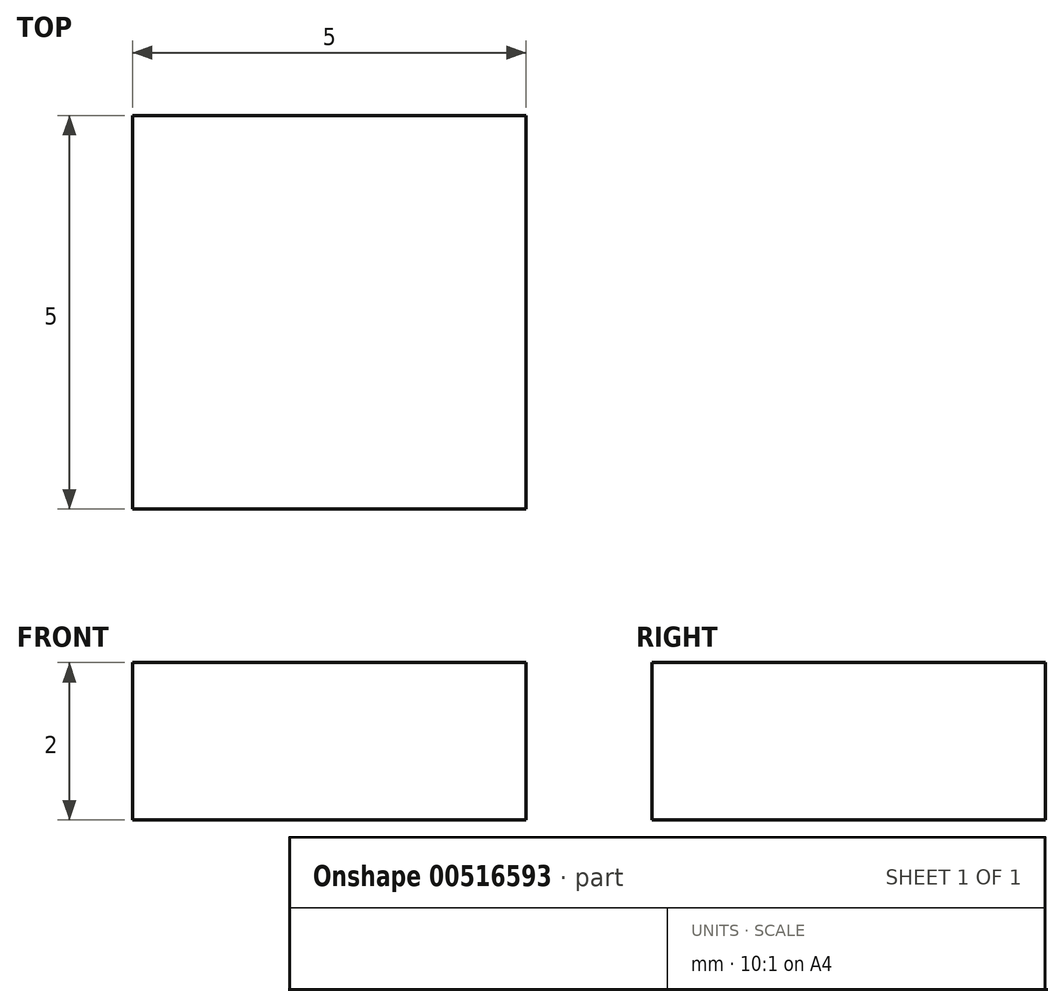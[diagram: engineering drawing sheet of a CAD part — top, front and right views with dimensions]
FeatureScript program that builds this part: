
annotation { "Feature Type Name" : "Feature", "Feature Type Description" : "" }
export const myFeature = defineFeature(function(context is Context, id is Id, definition is map)
    precondition{}
    {
        {
            var Q0;
            Q0=qCreatedBy(makeId("Top.planeOp"),FACE);
            var sketch = newSketch(context, id + "F0", { "sketchPlane" : qUnion([Q0])});
            skLineSegment(sketch, "E0.bottom", {"start": v(-2.5, 2.5) * mm, "end": v(2.5, 2.5) * mm});
            skLineSegment(sketch, "E0.top", {"start": v(-2.5, -2.5) * mm, "end": v(2.5, -2.5) * mm});
            skLineSegment(sketch, "E0.left", {"start": v(-2.5, 2.5) * mm, "end": v(-2.5, -2.5) * mm});
            skLineSegment(sketch, "E0.right", {"start": v(2.5, 2.5) * mm, "end": v(2.5, -2.5) * mm});
            skSolve(sketch);
        }
        {
            var Q0;
            Q0=makeQuery(id+"F0.imprint","IMPRINT",FACE,{"disambiguationData":[TD([[makeQuery(id+"F0.imprint","IMPRINT",EDGE,{"derivedFrom":sQuery(id+"F0.wireOp",EDGE,"E0.bottom")}),-1.0]])]});
            extrude(context, id + "F1", {"entities" : qUnion([Q0]), "depth" : 2 * mm, "offsetDistance" : 25 * mm});
        }
    });
